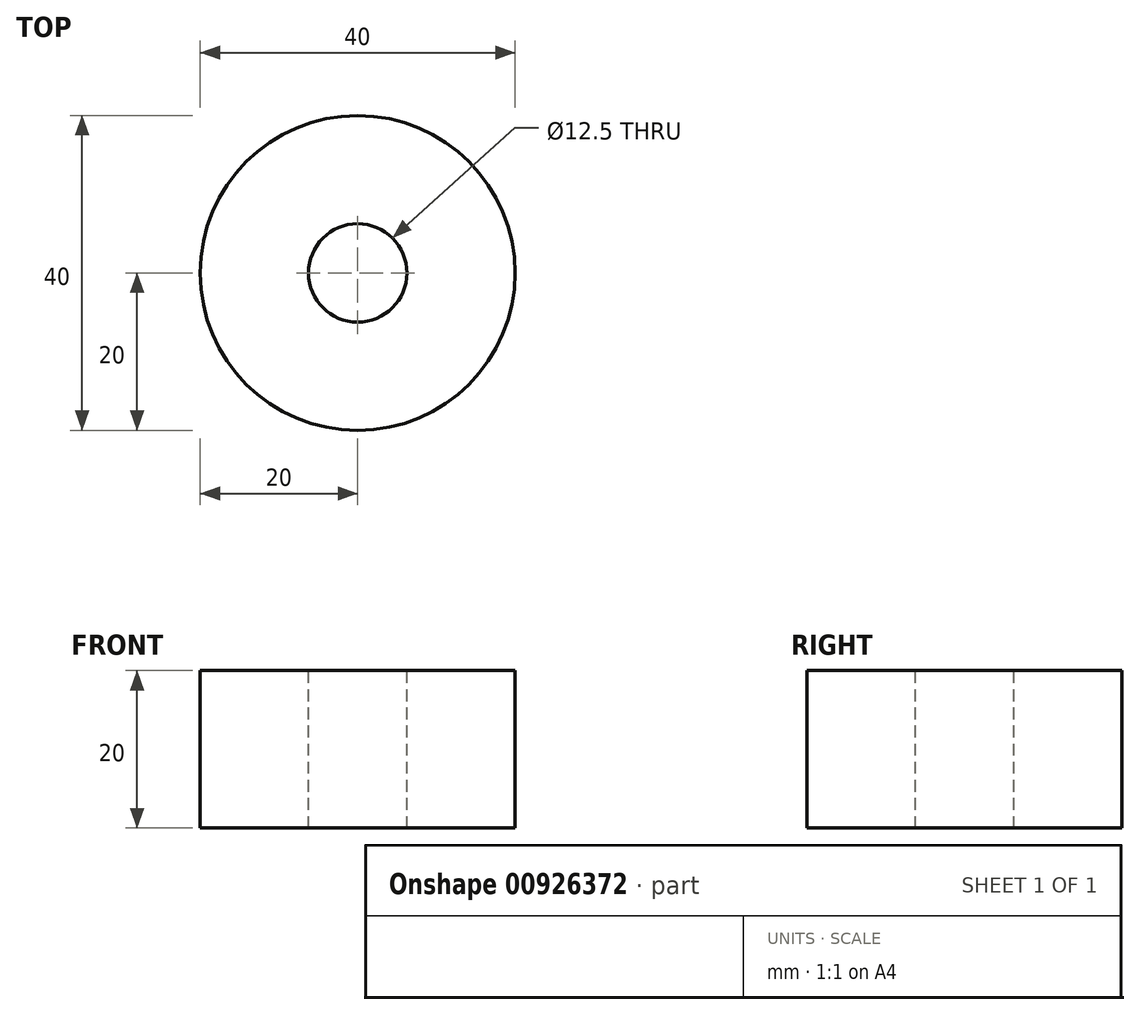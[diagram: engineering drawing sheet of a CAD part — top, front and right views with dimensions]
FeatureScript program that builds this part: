
annotation { "Feature Type Name" : "Feature", "Feature Type Description" : "" }
export const myFeature = defineFeature(function(context is Context, id is Id, definition is map)
    precondition{}
    {
        {
            var Q0;
            Q0=qCreatedBy(makeId("Top.planeOp"),FACE);
            var sketch = newSketch(context, id + "F0", { "sketchPlane" : qUnion([Q0])});
            skCircle(sketch, "E0", {"center": v(0, 0) * mm, "radius": 20 * mm});
            skSolve(sketch);
        }
        {
            var Q0;
            Q0 = qSketchRegion(id + "F0", true);
            extrude(context, id + "F1", {"entities" : qUnion([Q0]), "depth" : 20 * mm, "offsetDistance" : 25 * mm});
        }
        {
            var Q0;
            Q0=sQuery(id+"F0.wireOp",VERTEX,"E0.center");
            var Q1;
            Q1=makeQuery(id+"F1.opExtrude","SWEPT_BODY",BODY,{"disambiguationData":[OSD([sQuery(id+"F0.wireOp",EDGE,"E0")])]});
            hole(context, id + "F2", {"style" : HoleStyle.SIMPLE, "endStyle" : HoleEndStyle.THROUGH, "oppositeDirection" : true, "standardTappedOrClearance" : lookupTablePath({ "standard" : "ISO", "engagement" : "75%", "pitch" : "1.5 mm", "size" : "M14", "type" : "Tapped" }), "standardBlindInLast" : lookupTablePath({ "standard" : "ISO", "engagement" : "75%", "pitch" : "1.5 mm", "size" : "M14", "type" : "Tapped" }), "holeDiameter" : 12.5 * mm, "majorDiameter" : 14 * mm, "showTappedDepth" : true, "isTappedThrough" : true, "tappedDepth" : 12 * mm, "tapClearance" : 3, "startFromSketch" : true, "locations" : qUnion([Q0]), "scope" : qUnion([Q1])});
        }
    });
